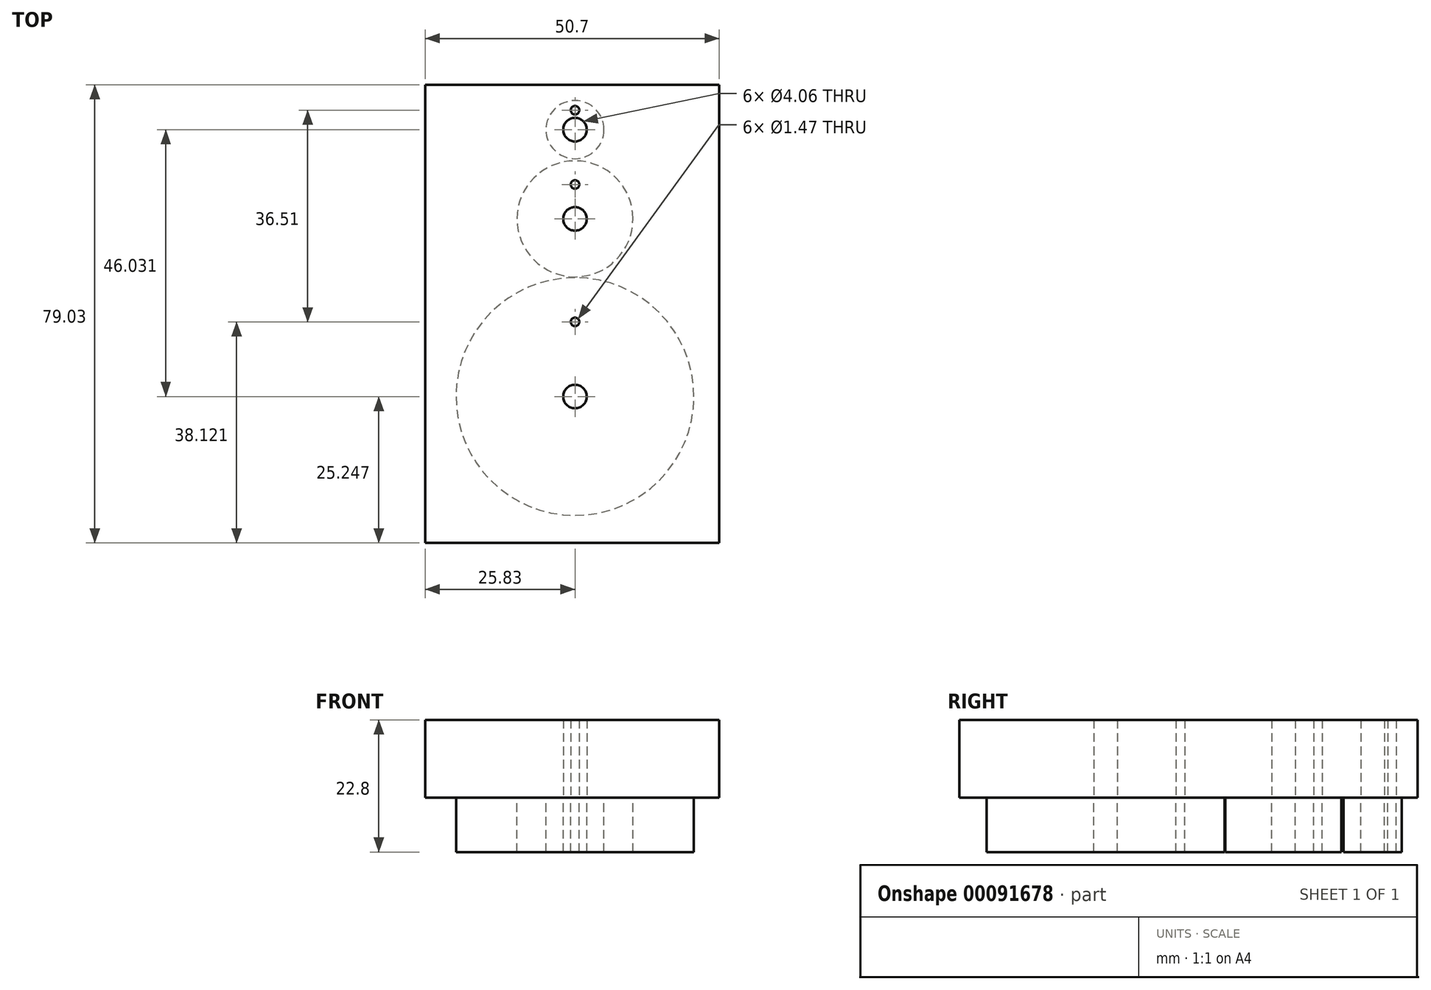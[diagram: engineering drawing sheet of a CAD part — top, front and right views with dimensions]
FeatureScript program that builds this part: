
annotation { "Feature Type Name" : "Feature", "Feature Type Description" : "" }
export const myFeature = defineFeature(function(context is Context, id is Id, definition is map)
    precondition{}
    {
        {
            var Q0;
            Q0=qCreatedBy(makeId("Top.planeOp"),FACE);
            var sketch = newSketch(context, id + "F0", { "sketchPlane" : qUnion([Q0])});
            skCircle(sketch, "E0", {"center": v(0, 15.39) * mm, "radius": 5 * mm});
            skCircle(sketch, "E1", {"center": v(0, -30.64) * mm, "radius": 20.5 * mm});
            skCircle(sketch, "E2", {"center": v(0, 0) * mm, "radius": 10 * mm});
            skLineSegment(sketch, "E3.bottom", {"start": v(-25.83, -55.89) * mm, "end": v(24.87, -55.89) * mm});
            skLineSegment(sketch, "E3.top", {"start": v(-25.83, 23.14) * mm, "end": v(24.87, 23.14) * mm});
            skLineSegment(sketch, "E3.left", {"start": v(-25.83, -55.89) * mm, "end": v(-25.83, 23.14) * mm});
            skLineSegment(sketch, "E3.right", {"start": v(24.87, -55.89) * mm, "end": v(24.87, 23.14) * mm});
            skCircle(sketch, "E4", {"center": v(0, -30.64) * mm, "radius": 2.03 * mm});
            skCircle(sketch, "E5", {"center": v(0, 0) * mm, "radius": 2.03 * mm});
            skCircle(sketch, "E6", {"center": v(0, 15.39) * mm, "radius": 2.03 * mm});
            skCircle(sketch, "E7", {"center": v(0, -17.77) * mm, "radius": 0.73 * mm});
            skCircle(sketch, "E8", {"center": v(0, 5.94) * mm, "radius": 0.74 * mm});
            skCircle(sketch, "E9", {"center": v(0, 18.74) * mm, "radius": 0.73 * mm});
            skSolve(sketch);
        }
        {
            var Q0;
            Q0=makeQuery(id+"F0.imprint","IMPRINT",FACE,{"disambiguationData":[TD([[makeQuery(id+"F0.imprint","IMPRINT",EDGE,{"derivedFrom":sQuery(id+"F0.wireOp",EDGE,"E0")}),1.0]])]});
            var Q1;
            Q1=makeQuery(id+"F0.imprint","IMPRINT",FACE,{"disambiguationData":[TD([[makeQuery(id+"F0.imprint","IMPRINT",EDGE,{"derivedFrom":sQuery(id+"F0.wireOp",EDGE,"E2")}),1.0]])]});
            var Q2;
            Q2=makeQuery(id+"F0.imprint","IMPRINT",FACE,{"disambiguationData":[TD([[makeQuery(id+"F0.imprint","IMPRINT",EDGE,{"derivedFrom":sQuery(id+"F0.wireOp",EDGE,"E1")}),1.0]])]});
            extrude(context, id + "F1", {"entities" : qUnion([Q0, Q1, Q2]), "oppositeDirection" : true, "depth" : 9.4 * mm});
        }
        {
            var Q0;
            Q0=makeQuery(id+"F0.imprint","IMPRINT",FACE,{"disambiguationData":[TD([[makeQuery(id+"F0.imprint","IMPRINT",EDGE,{"derivedFrom":sQuery(id+"F0.wireOp",EDGE,"E0")}),-1.0]])]});
            var Q1;
            Q1=makeQuery(id+"F0.imprint","IMPRINT",FACE,{"disambiguationData":[TD([[makeQuery(id+"F0.imprint","IMPRINT",EDGE,{"derivedFrom":sQuery(id+"F0.wireOp",EDGE,"E2")}),1.0]])]});
            var Q2;
            Q2=makeQuery(id+"F0.imprint","IMPRINT",FACE,{"disambiguationData":[TD([[makeQuery(id+"F0.imprint","IMPRINT",EDGE,{"derivedFrom":sQuery(id+"F0.wireOp",EDGE,"E1")}),1.0]])]});
            var Q3;
            Q3=makeQuery(id+"F0.imprint","IMPRINT",FACE,{"disambiguationData":[TD([[makeQuery(id+"F0.imprint","IMPRINT",EDGE,{"derivedFrom":sQuery(id+"F0.wireOp",EDGE,"E0")}),1.0]])]});
            extrude(context, id + "F2", {"entities" : qUnion([Q0, Q1, Q2, Q3]), "depth" : 13.4 * mm});
        }
    });
